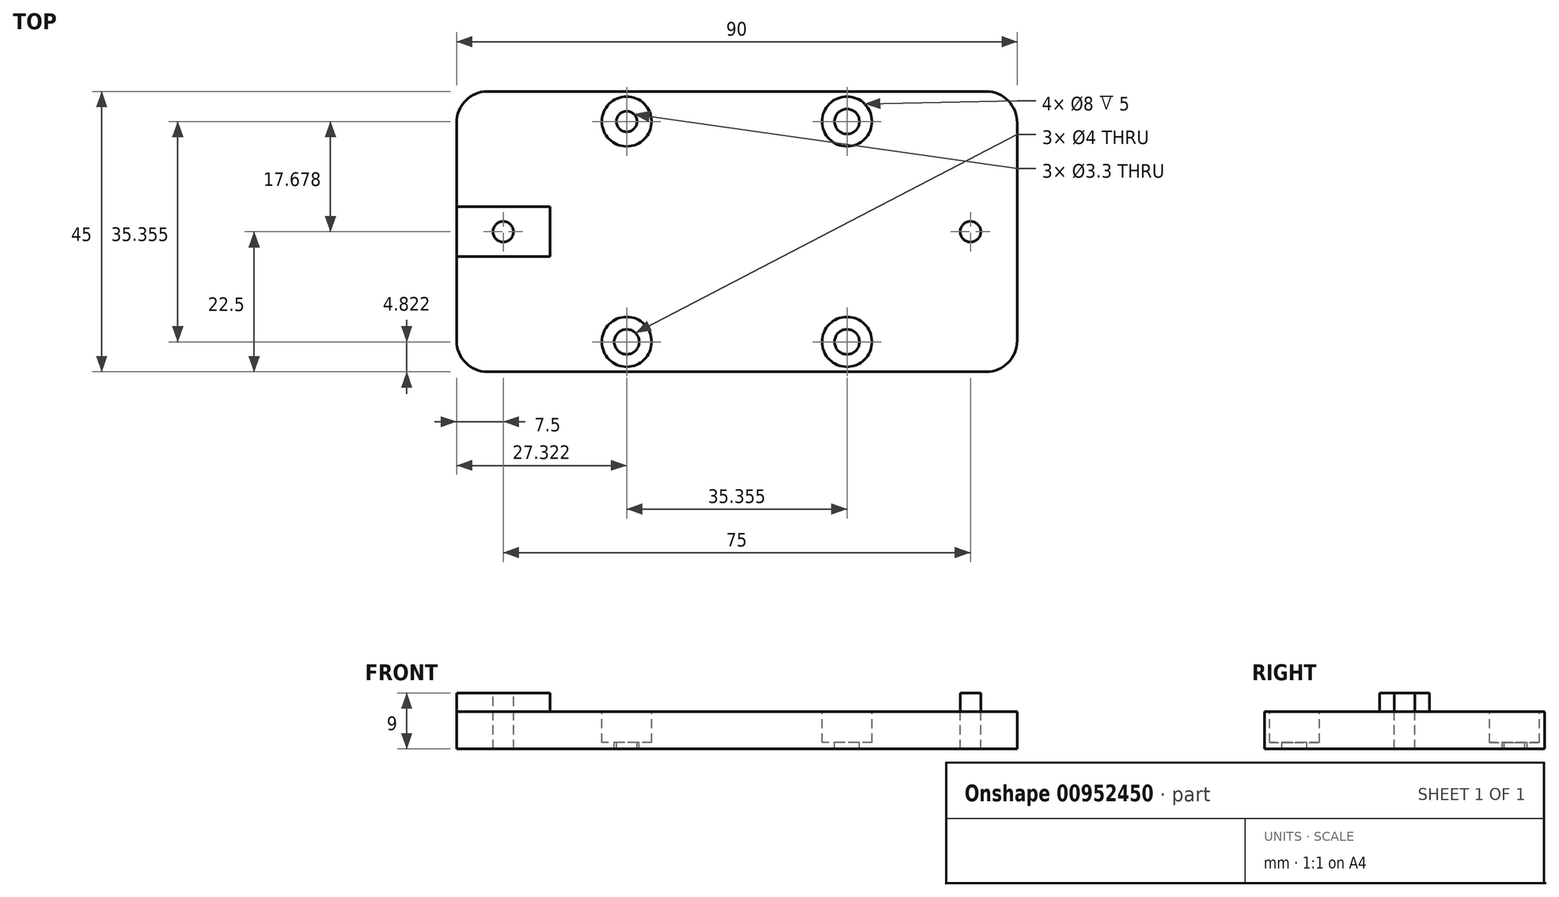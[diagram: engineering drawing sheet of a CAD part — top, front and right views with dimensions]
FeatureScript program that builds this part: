
annotation { "Feature Type Name" : "Feature", "Feature Type Description" : "" }
export const myFeature = defineFeature(function(context is Context, id is Id, definition is map)
    precondition{}
    {
        {
            var Q0;
            Q0=qCreatedBy(makeId("Top.planeOp"),FACE);
            var sketch = newSketch(context, id + "F0", { "sketchPlane" : qUnion([Q0])});
            skLineSegment(sketch, "E0.bottom", {"start": v(-40, 22.5) * mm, "end": v(40, 22.5) * mm});
            skLineSegment(sketch, "E0.top", {"start": v(-40, -22.5) * mm, "end": v(40, -22.5) * mm});
            skLineSegment(sketch, "E0.left", {"start": v(-45, 17.5) * mm, "end": v(-45, -17.5) * mm});
            skLineSegment(sketch, "E0.right", {"start": v(45, 17.5) * mm, "end": v(45, -17.5) * mm});
            skPoint(sketch, "E0.middle", {"position": v(0, 0) * mm});
            skCircle(sketch, "E1.1.0", {"center": v(-17.68, 17.68) * mm, "radius": 4 * mm});
            skCircle(sketch, "E1.1.1", {"center": v(-17.68, 17.68) * mm, "radius": 1.65 * mm});
            skCircle(sketch, "E1.3.0", {"center": v(-17.68, -17.68) * mm, "radius": 4 * mm});
            skCircle(sketch, "E1.3.1", {"center": v(-17.68, -17.68) * mm, "radius": 2 * mm});
            skPoint(sketch, "E2.visualSharp", {"position": v(-45, 22.5) * mm});
            skArc(sketch, "E2.filletArc", {"start": v(-40, 22.5) * mm, "mid": v(-43.54, 21.04) * mm, "end": v(-45, 17.5) * mm});
            skPoint(sketch, "E3.visualSharp", {"position": v(45, 22.5) * mm});
            skArc(sketch, "E3.filletArc", {"start": v(45, 17.5) * mm, "mid": v(43.54, 21.04) * mm, "end": v(40, 22.5) * mm});
            skPoint(sketch, "E4.visualSharp", {"position": v(45, -22.5) * mm});
            skArc(sketch, "E4.filletArc", {"start": v(40, -22.5) * mm, "mid": v(43.54, -21.04) * mm, "end": v(45, -17.5) * mm});
            skPoint(sketch, "E5.visualSharp", {"position": v(-45, -22.5) * mm});
            skArc(sketch, "E5.filletArc", {"start": v(-45, -17.5) * mm, "mid": v(-43.54, -21.04) * mm, "end": v(-40, -22.5) * mm});
            skCircle(sketch, "E6.1.5.0", {"center": v(17.68, -17.68) * mm, "radius": 4 * mm});
            skCircle(sketch, "E6.2.5.0", {"center": v(17.68, -17.68) * mm, "radius": 2 * mm});
            skCircle(sketch, "E6.1.7.0", {"center": v(17.68, 17.68) * mm, "radius": 4 * mm});
            skCircle(sketch, "E6.2.7.0", {"center": v(17.68, 17.68) * mm, "radius": 2 * mm});
            skCircle(sketch, "E7", {"center": v(-37.5, 0) * mm, "radius": 1.65 * mm});
            skCircle(sketch, "E8.MirrorC", {"center": v(37.5, 0) * mm, "radius": 1.65 * mm});
            skLineSegment(sketch, "E9", {"start": v(-45, 4) * mm, "end": v(-30, 4) * mm});
            skLineSegment(sketch, "E10", {"start": v(-30, 4) * mm, "end": v(-30, 0) * mm});
            skLineSegment(sketch, "E11.MirrorCS", {"start": v(-45, -4) * mm, "end": v(-30, -4) * mm});
            skLineSegment(sketch, "E12.MirrorCS", {"start": v(-30, -4) * mm, "end": v(-30, 0) * mm});
            skLineSegment(sketch, "E13.MirrorCS", {"start": v(45, 4) * mm, "end": v(30, 4) * mm});
            skLineSegment(sketch, "E14.MirrorCS", {"start": v(30, 4) * mm, "end": v(30, 0) * mm});
            skLineSegment(sketch, "E15.MirrorCS", {"start": v(30, -4) * mm, "end": v(30, 0) * mm});
            skLineSegment(sketch, "E16.MirrorCS", {"start": v(45, -4) * mm, "end": v(30, -4) * mm});
            skSolve(sketch);
        }
        {
            var Q0;
            Q0=qSketchRegion(id+"F0",true);
            var Q1;
            Q1=makeQuery(id+"F0.imprint","IMPRINT",FACE,{"disambiguationData":[TD([[makeQuery(id+"F0.imprint","IMPRINT",EDGE,{"derivedFrom":sQuery(id+"F0.wireOp",EDGE,"E1.1.0")}),1.0]])]});
            var Q2;
            Q2=makeQuery(id+"F0.imprint","IMPRINT",FACE,{"disambiguationData":[TD([[makeQuery(id+"F0.imprint","IMPRINT",EDGE,{"derivedFrom":sQuery(id+"F0.wireOp",EDGE,"UzwqMxC6-Xfvl-kvK5-6X4W-a8Wug1Xq9vTY")}),-1.0]])]});
            var Q3;
            Q3=makeQuery(id+"F0.imprint","IMPRINT",FACE,{"disambiguationData":[TD([[makeQuery(id+"F0.imprint","IMPRINT",EDGE,{"derivedFrom":sQuery(id+"F0.wireOp",EDGE,"E1.3.0")}),1.0]])]});
            var Q4;
            Q4=makeQuery(id+"F0.imprint","IMPRINT",FACE,{"disambiguationData":[TD([[makeQuery(id+"F0.imprint","IMPRINT",EDGE,{"derivedFrom":sQuery(id+"F0.wireOp",EDGE,"E1.2.0")}),1.0]])]});
            var Q5;
            Q5=makeQuery(id+"F0.imprint","IMPRINT",FACE,{"disambiguationData":[TD([[makeQuery(id+"F0.imprint","IMPRINT",EDGE,{"derivedFrom":sQuery(id+"F0.wireOp",EDGE,"E6.1.7.0")}),1.0]])]});
            var Q6;
            Q6=makeQuery(id+"F0.imprint","IMPRINT",FACE,{"disambiguationData":[TD([[makeQuery(id+"F0.imprint","IMPRINT",EDGE,{"derivedFrom":sQuery(id+"F0.wireOp",EDGE,"E6.1.5.0")}),1.0]])]});
            var Q7;
            Q7=makeQuery(id+"F0.imprint","IMPRINT",FACE,{"disambiguationData":[TD([[makeQuery(id+"F0.imprint","IMPRINT",EDGE,{"derivedFrom":sQuery(id+"F0.wireOp",EDGE,"E6.1.4.0")}),1.0]])]});
            extrude(context, id + "F1", {"entities" : qUnion([Q0, Q1, Q2, Q3, Q4, Q5, Q6, Q7]), "oppositeDirection" : true, "depth" : 6 * mm, "offsetDistance" : 25 * mm});
        }
        {
            var Q0;
            Q0=makeQuery(id+"F0.imprint","IMPRINT",FACE,{"disambiguationData":[TD([[makeQuery(id+"F0.imprint","IMPRINT",EDGE,{"derivedFrom":sQuery(id+"F0.wireOp",EDGE,"E1.1.0")}),1.0]])]});
            var Q1;
            Q1=makeQuery(id+"F0.imprint","IMPRINT",FACE,{"disambiguationData":[TD([[makeQuery(id+"F0.imprint","IMPRINT",EDGE,{"derivedFrom":sQuery(id+"F0.wireOp",EDGE,"E1.1.1")}),1.0]])]});
            var Q2;
            Q2=makeQuery(id+"F0.imprint","IMPRINT",FACE,{"disambiguationData":[TD([[makeQuery(id+"F0.imprint","IMPRINT",EDGE,{"derivedFrom":sQuery(id+"F0.wireOp",EDGE,"UzwqMxC6-Xfvl-kvK5-6X4W-a8Wug1Xq9vTY")}),-1.0]])]});
            var Q3;
            Q3=makeQuery(id+"F0.imprint","IMPRINT",FACE,{"disambiguationData":[TD([[makeQuery(id+"F0.imprint","IMPRINT",EDGE,{"derivedFrom":sQuery(id+"F0.wireOp",EDGE,"E1.2.0")}),1.0]])]});
            var Q4;
            Q4=makeQuery(id+"F0.imprint","IMPRINT",FACE,{"disambiguationData":[TD([[makeQuery(id+"F0.imprint","IMPRINT",EDGE,{"derivedFrom":sQuery(id+"F0.wireOp",EDGE,"E1.3.0")}),1.0]])]});
            var Q5;
            Q5=makeQuery(id+"F0.imprint","IMPRINT",FACE,{"disambiguationData":[TD([[makeQuery(id+"F0.imprint","IMPRINT",EDGE,{"derivedFrom":sQuery(id+"F0.wireOp",EDGE,"E6.1.4.0")}),1.0]])]});
            var Q6;
            Q6=makeQuery(id+"F0.imprint","IMPRINT",FACE,{"disambiguationData":[TD([[makeQuery(id+"F0.imprint","IMPRINT",EDGE,{"derivedFrom":sQuery(id+"F0.wireOp",EDGE,"E6.1.5.0")}),1.0]])]});
            var Q7;
            Q7=makeQuery(id+"F0.imprint","IMPRINT",FACE,{"disambiguationData":[TD([[makeQuery(id+"F0.imprint","IMPRINT",EDGE,{"derivedFrom":sQuery(id+"F0.wireOp",EDGE,"E6.1.7.0")}),1.0]])]});
            extrude(context, id + "F2", {"entities" : qUnion([Q0, Q1, Q2, Q3, Q4, Q5, Q6, Q7]), "operationType" : NewBodyOperationType.REMOVE, "oppositeDirection" : true, "depth" : 5 * mm, "offsetDistance" : 25 * mm});
        }
        {
            var Q0;
            Q0=makeQuery(id+"F0.imprint","IMPRINT",FACE,{"disambiguationData":[TD([[makeQuery(id+"F0.imprint","IMPRINT",EDGE,{"derivedFrom":sQuery(id+"F0.wireOp",EDGE,"E7")}),-1.0]])]});
            var Q1;
            Q1=makeQuery(id+"F0.imprint","IMPRINT",FACE,{"disambiguationData":[TD([[makeQuery(id+"F0.imprint","IMPRINT",EDGE,{"derivedFrom":sQuery(id+"F0.wireOp",EDGE,"E8.MirrorC")}),1.0]])]});
            extrude(context, id + "F3", {"entities" : qUnion([Q0, Q1]), "operationType" : NewBodyOperationType.ADD, "depth" : 3 * mm, "offsetDistance" : 25 * mm});
        }
    });
